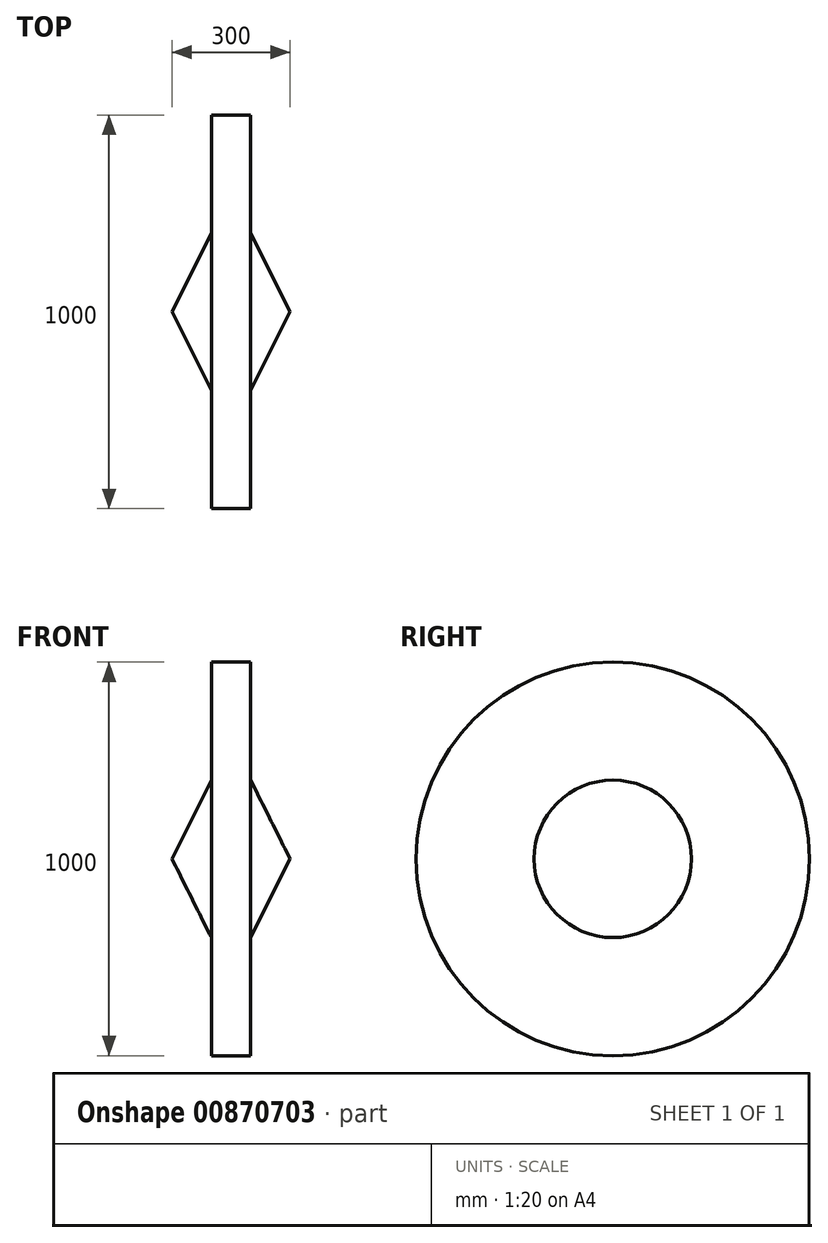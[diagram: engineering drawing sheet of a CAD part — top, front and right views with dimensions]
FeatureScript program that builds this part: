
annotation { "Feature Type Name" : "Feature", "Feature Type Description" : "" }
export const myFeature = defineFeature(function(context is Context, id is Id, definition is map)
    precondition{}
    {
        {
            var Q0;
            Q0=qCreatedBy(makeId("Front.planeOp"),FACE);
            var sketch = newSketch(context, id + "F0", { "sketchPlane" : qUnion([Q0])});
            skLineSegment(sketch, "E0", {"start": v(0, 500) * mm, "end": v(150, 500) * mm});
            skLineSegment(sketch, "E1", {"start": v(0, 0) * mm, "end": v(50, 0) * mm});
            skLineSegment(sketch, "E2", {"start": v(50, 0) * mm, "end": v(50, 300) * mm});
            skLineSegment(sketch, "E3", {"start": v(50, 300) * mm, "end": v(150, 500) * mm});
            skLineSegment(sketch, "E4.MirrorCS", {"start": v(0, 500) * mm, "end": v(-150, 500) * mm});
            skLineSegment(sketch, "E5.MirrorCS", {"start": v(-50, 300) * mm, "end": v(-150, 500) * mm});
            skLineSegment(sketch, "E6.MirrorCS", {"start": v(-50, 0) * mm, "end": v(-50, 300) * mm});
            skLineSegment(sketch, "E7.MirrorCS", {"start": v(0, 0) * mm, "end": v(-50, 0) * mm});
            skSolve(sketch);
        }
        {
            var Q0;
            Q0=makeQuery(id+"F0.imprint","IMPRINT",FACE,{"disambiguationData":[TD([[makeQuery(id+"F0.imprint","IMPRINT",EDGE,{"derivedFrom":sQuery(id+"F0.wireOp",EDGE,"E0")}),-1.0]])]});
            var Q1;
            Q1=sQuery(id+"F0.wireOp",EDGE,"E4.MirrorCS");
            revolve(context, id + "F1", {"surfaceOperationType" : NewSurfaceOperationType.NEW, "entities" : qUnion([Q0]), "axis" : qUnion([Q1]), "revolveType" : RevolveType.FULL});
        }
    });
